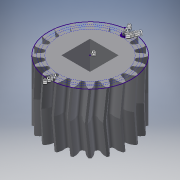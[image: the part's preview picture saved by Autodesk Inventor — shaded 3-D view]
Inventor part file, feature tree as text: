
AUTODESK INVENTOR PART (.ipt)
format: ipt  version: 2017 (Build 210142000, 142)  size: 705,536 bytes
history: native  units: mm
features: sketch x3, extrude x3, pattern_circular x2, helix x2, projected_geometry x1
ambient origin geometry x8: Origin, YZ Plane, XZ Plane, XY Plane, X Axis, Y Axis, Z Axis, Center Point
bodies: Solid1 (feature_tree)
feature tree (11):
  sketch  "Sketch1"  dims[d0=20.0mm d1=0.0mm]
  extrude  "Extrusion1"  TaperAngle=0.0deg  [1 undecoded]
  extrude  "Extrusion2"  Depth=200.0mm TaperAngle=360.0deg
  pattern_circular  "Circular Pattern1"  [2 undecoded]
  extrude  "Extrusion3"  Depth=200.0mm TaperAngle=360.0deg
  helix  "Coil1"  [1 undecoded]
  helix  "Coil2"  [1 undecoded]
  pattern_circular  "Circular Pattern2"  [2 undecoded]
  sketch  "Sketch2"  dims[d2=10.0mm d3=0.0mm d4=200.0mm d5=360.0deg]
  sketch  "Sketch3"  dims[d7=9.525mm d8=10.0mm d9=0.0mm d10=10.0mm d11=10.0mm d12=0.1mm d13=0.0mm d14=90.0deg d15=90.0deg d16=0.0mm d17=0.0mm d18=10.0mm d19=10.0mm d20=0.1mm d21=0.0mm d22=90.0deg d23=90.0deg d24=0.0mm d25=0.0mm d26=200.0mm d27=360.0deg]
  projected_geometry  "Projected Loop1"
note: 7 required parameter values undecoded (feature->parameter linkage not recoverable at this tier; creation-order binding heuristic only, values carry confidence <= 0.55)
